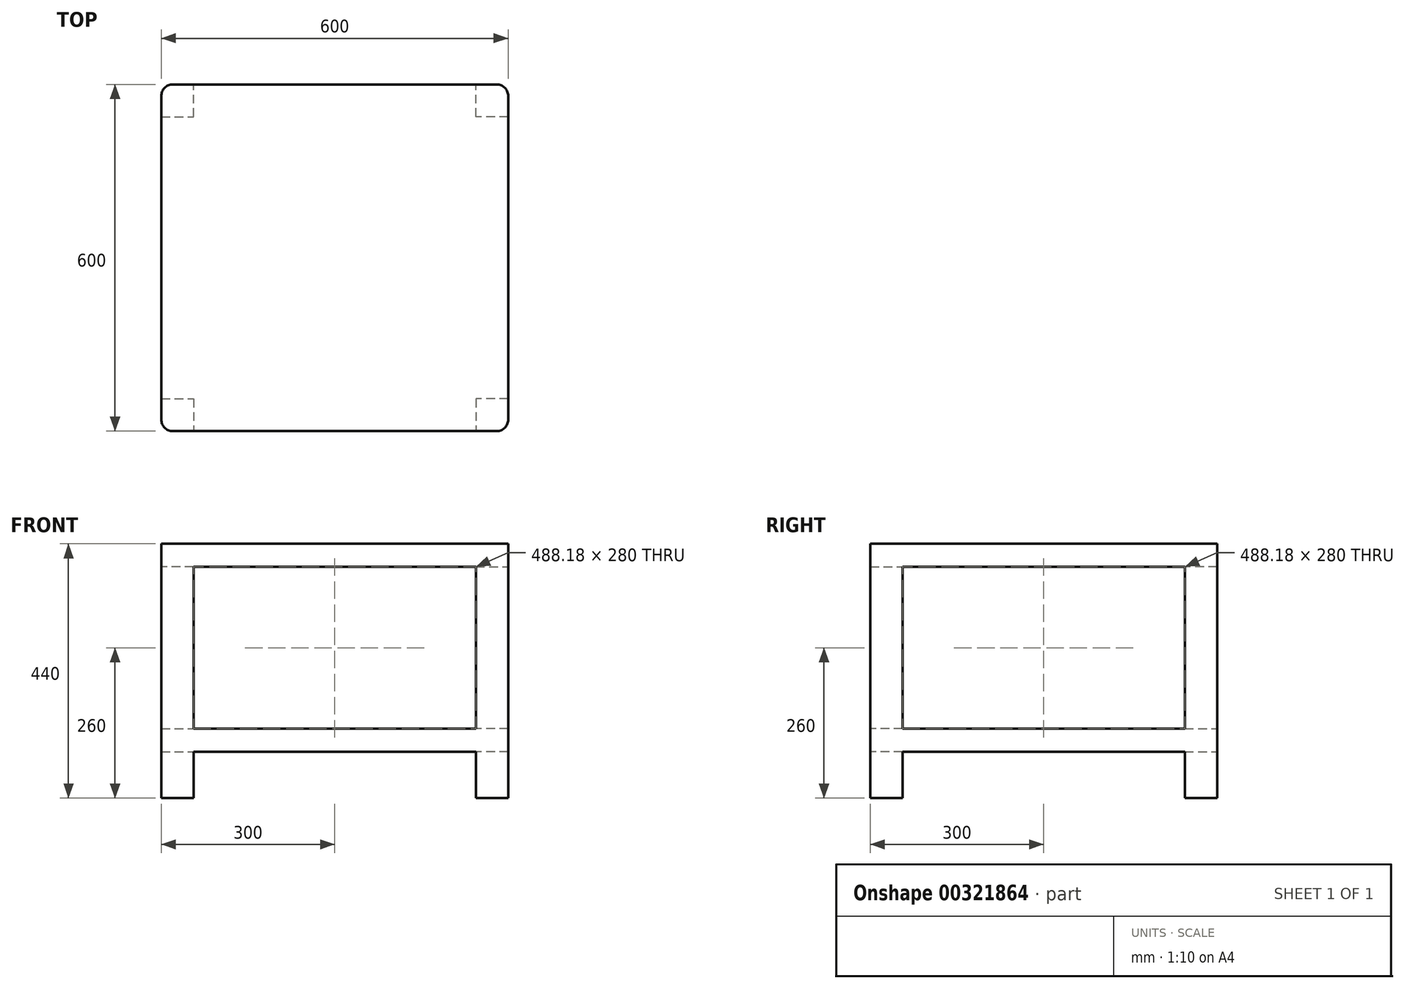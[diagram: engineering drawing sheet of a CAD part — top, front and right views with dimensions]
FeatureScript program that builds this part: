
annotation { "Feature Type Name" : "Feature", "Feature Type Description" : "" }
export const myFeature = defineFeature(function(context is Context, id is Id, definition is map)
    precondition{}
    {
        {
            var Q0;
            Q0=qCreatedBy(makeId("Top.planeOp"),FACE);
            var sketch = newSketch(context, id + "F0", { "sketchPlane" : qUnion([Q0])});
            skLineSegment(sketch, "E0.bottom", {"start": v(300, -300) * mm, "end": v(-300, -300) * mm});
            skLineSegment(sketch, "E0.top", {"start": v(300, 300) * mm, "end": v(-300, 300) * mm});
            skLineSegment(sketch, "E0.left", {"start": v(300, -300) * mm, "end": v(300, 300) * mm});
            skLineSegment(sketch, "E0.right", {"start": v(-300, -300) * mm, "end": v(-300, 300) * mm});
            skPoint(sketch, "E0.middle", {"position": v(0, 0) * mm});
            skSolve(sketch);
        }
        {
            var Q0;
            Q0=makeQuery(id+"F0.imprint","IMPRINT",FACE,{"disambiguationData":[TD([[makeQuery(id+"F0.imprint","IMPRINT",EDGE,{"derivedFrom":sQuery(id+"F0.wireOp",EDGE,"E0.bottom")}),-1.0]])]});
            extrude(context, id + "F1", {"entities" : qUnion([Q0]), "depth" : 40 * mm});
        }
        {
            var Q0;
            Q0=makeQuery(id+"F1.opExtrude","CAP_FACE",FACE,{"disambiguationData":[OSD([sQuery(id+"F0.wireOp",EDGE,"E0.bottom"),sQuery(id+"F0.wireOp",EDGE,"E0.top"),sQuery(id+"F0.wireOp",EDGE,"E0.left"),sQuery(id+"F0.wireOp",EDGE,"E0.right")])],"isStart":true});
            var sketch = newSketch(context, id + "F2", { "sketchPlane" : qUnion([Q0])});
            skLineSegment(sketch, "E1", {"start": v(-300, 0) * mm, "end": v(300, 0) * mm, "construction": true});
            skLineSegment(sketch, "E2", {"start": v(0, -300) * mm, "end": v(0, 300) * mm, "construction": true});
            skLineSegment(sketch, "E3.bottom", {"start": v(-244.09, 300) * mm, "end": v(-300, 300) * mm});
            skLineSegment(sketch, "E3.top", {"start": v(-244.09, 244.09) * mm, "end": v(-300, 244.09) * mm});
            skLineSegment(sketch, "E3.left", {"start": v(-244.09, 300) * mm, "end": v(-244.09, 244.09) * mm});
            skLineSegment(sketch, "E3.right", {"start": v(-300, 300) * mm, "end": v(-300, 244.09) * mm});
            skPoint(sketch, "E3.middle", {"position": v(-272.04, 272.04) * mm});
            skLineSegment(sketch, "E4.MirrorCS", {"start": v(244.09, 244.09) * mm, "end": v(300, 244.09) * mm});
            skLineSegment(sketch, "E5.MirrorCS", {"start": v(300, 300) * mm, "end": v(300, 244.09) * mm});
            skLineSegment(sketch, "E6.MirrorCS", {"start": v(244.09, 300) * mm, "end": v(244.09, 244.09) * mm});
            skLineSegment(sketch, "E7.MirrorCS", {"start": v(244.09, 300) * mm, "end": v(300, 300) * mm});
            skLineSegment(sketch, "E8.MirrorCS", {"start": v(300, -300) * mm, "end": v(300, -244.09) * mm});
            skLineSegment(sketch, "E9.MirrorCS", {"start": v(244.09, -300) * mm, "end": v(300, -300) * mm});
            skLineSegment(sketch, "E10.MirrorCS", {"start": v(244.09, -300) * mm, "end": v(244.09, -244.09) * mm});
            skLineSegment(sketch, "E11.MirrorCS", {"start": v(244.09, -244.09) * mm, "end": v(300, -244.09) * mm});
            skLineSegment(sketch, "E12.MirrorCS", {"start": v(-244.09, -244.09) * mm, "end": v(-300, -244.09) * mm});
            skLineSegment(sketch, "E13.MirrorCS", {"start": v(-300, -300) * mm, "end": v(-300, -244.09) * mm});
            skLineSegment(sketch, "E14.MirrorCS", {"start": v(-244.09, -300) * mm, "end": v(-244.09, -244.09) * mm});
            skLineSegment(sketch, "E15.MirrorCS", {"start": v(-244.09, -300) * mm, "end": v(-300, -300) * mm});
            skSolve(sketch);
        }
        {
            var Q0;
            Q0 = qSketchRegion(id + "F2", true);
            extrude(context, id + "F3", {"entities" : qUnion([Q0]), "operationType" : NewBodyOperationType.ADD, "depth" : 400 * mm});
        }
        {
            var Q0;
            Q0=makeQuery(id+"F1.opExtrude","CAP_FACE",FACE,{"disambiguationData":[OSD([sQuery(id+"F0.wireOp",EDGE,"E0.bottom"),sQuery(id+"F0.wireOp",EDGE,"E0.top"),sQuery(id+"F0.wireOp",EDGE,"E0.left"),sQuery(id+"F0.wireOp",EDGE,"E0.right")])],"isStart":false});
            cPlane(context, id + "F4", {"entities" : qUnion([Q0]), "cplaneType" : CPlaneType.OFFSET, "offset" : 320 * mm, "oppositeDirection" : true, "width" : 150 * mm, "height" : 150 * mm});
        }
        {
            var Q0;
            Q0=qCreatedBy(id+"F4.planeOp",FACE);
            var sketch = newSketch(context, id + "F5", { "sketchPlane" : qUnion([Q0])});
            skLineSegment(sketch, "E16.0", {"start": v(-300, -300) * mm, "end": v(-300, 300) * mm});
            skLineSegment(sketch, "E17.0", {"start": v(300, 300) * mm, "end": v(-300, 300) * mm});
            skLineSegment(sketch, "E18.0", {"start": v(300, -300) * mm, "end": v(300, 300) * mm});
            skLineSegment(sketch, "E19.0", {"start": v(300, -300) * mm, "end": v(-300, -300) * mm});
            skSolve(sketch);
        }
        {
            var Q0;
            Q0=makeQuery(id+"F5.imprint","IMPRINT",FACE,{"disambiguationData":[TD([[makeQuery(id+"F5.imprint","IMPRINT",EDGE,{"derivedFrom":sQuery(id+"F5.wireOp",EDGE,"E16.0")}),-1.0]])]});
            extrude(context, id + "F6", {"entities" : qUnion([Q0]), "operationType" : NewBodyOperationType.ADD, "oppositeDirection" : true, "depth" : 40 * mm});
        }
        {
            var Q0;
            Q0=makeQuery(id+"F3.boolean.opBoolean","MERGE",EDGE,{"derivedFrom":[makeQuery(id+"F1.opExtrude","SWEPT_EDGE",EDGE,{"disambiguationData":[OSD([sQuery(id+"F0.wireOp",EDGE,"E0.bottom"),sQuery(id+"F0.wireOp",EDGE,"E0.left")])]}),makeQuery(id+"F3.opExtrude","SWEPT_EDGE",EDGE,{"disambiguationData":[OSD([sQuery(id+"F2.wireOp",EDGE,"E5.MirrorCS"),sQuery(id+"F2.wireOp",EDGE,"E7.MirrorCS")])]})]});
            var Q1;
            Q1=makeQuery(id+"F3.boolean.opBoolean","MERGE",EDGE,{"derivedFrom":[makeQuery(id+"F1.opExtrude","SWEPT_EDGE",EDGE,{"disambiguationData":[OSD([sQuery(id+"F0.wireOp",EDGE,"E0.bottom"),sQuery(id+"F0.wireOp",EDGE,"E0.right")])]}),makeQuery(id+"F3.opExtrude","SWEPT_EDGE",EDGE,{"disambiguationData":[OSD([sQuery(id+"F2.wireOp",EDGE,"E3.bottom"),sQuery(id+"F2.wireOp",EDGE,"E3.right")])]})]});
            var Q2;
            Q2=makeQuery(id+"F3.boolean.opBoolean","MERGE",EDGE,{"derivedFrom":[makeQuery(id+"F1.opExtrude","SWEPT_EDGE",EDGE,{"disambiguationData":[OSD([sQuery(id+"F0.wireOp",EDGE,"E0.top"),sQuery(id+"F0.wireOp",EDGE,"E0.left")])]}),makeQuery(id+"F3.opExtrude","SWEPT_EDGE",EDGE,{"disambiguationData":[OSD([sQuery(id+"F2.wireOp",EDGE,"E8.MirrorCS"),sQuery(id+"F2.wireOp",EDGE,"E9.MirrorCS")])]})]});
            var Q3;
            Q3=makeQuery(id+"F3.boolean.opBoolean","MERGE",EDGE,{"derivedFrom":[makeQuery(id+"F1.opExtrude","SWEPT_EDGE",EDGE,{"disambiguationData":[OSD([sQuery(id+"F0.wireOp",EDGE,"E0.top"),sQuery(id+"F0.wireOp",EDGE,"E0.right")])]}),makeQuery(id+"F3.opExtrude","SWEPT_EDGE",EDGE,{"disambiguationData":[OSD([sQuery(id+"F2.wireOp",EDGE,"E13.MirrorCS"),sQuery(id+"F2.wireOp",EDGE,"E15.MirrorCS")])]})]});
            fillet(context, id + "F7", {"entities" : qUnion([Q0, Q1, Q2, Q3]), "radius" : 20 * mm, "tangentPropagation" : true, "allowEdgeOverflow" : false});
        }
    });
